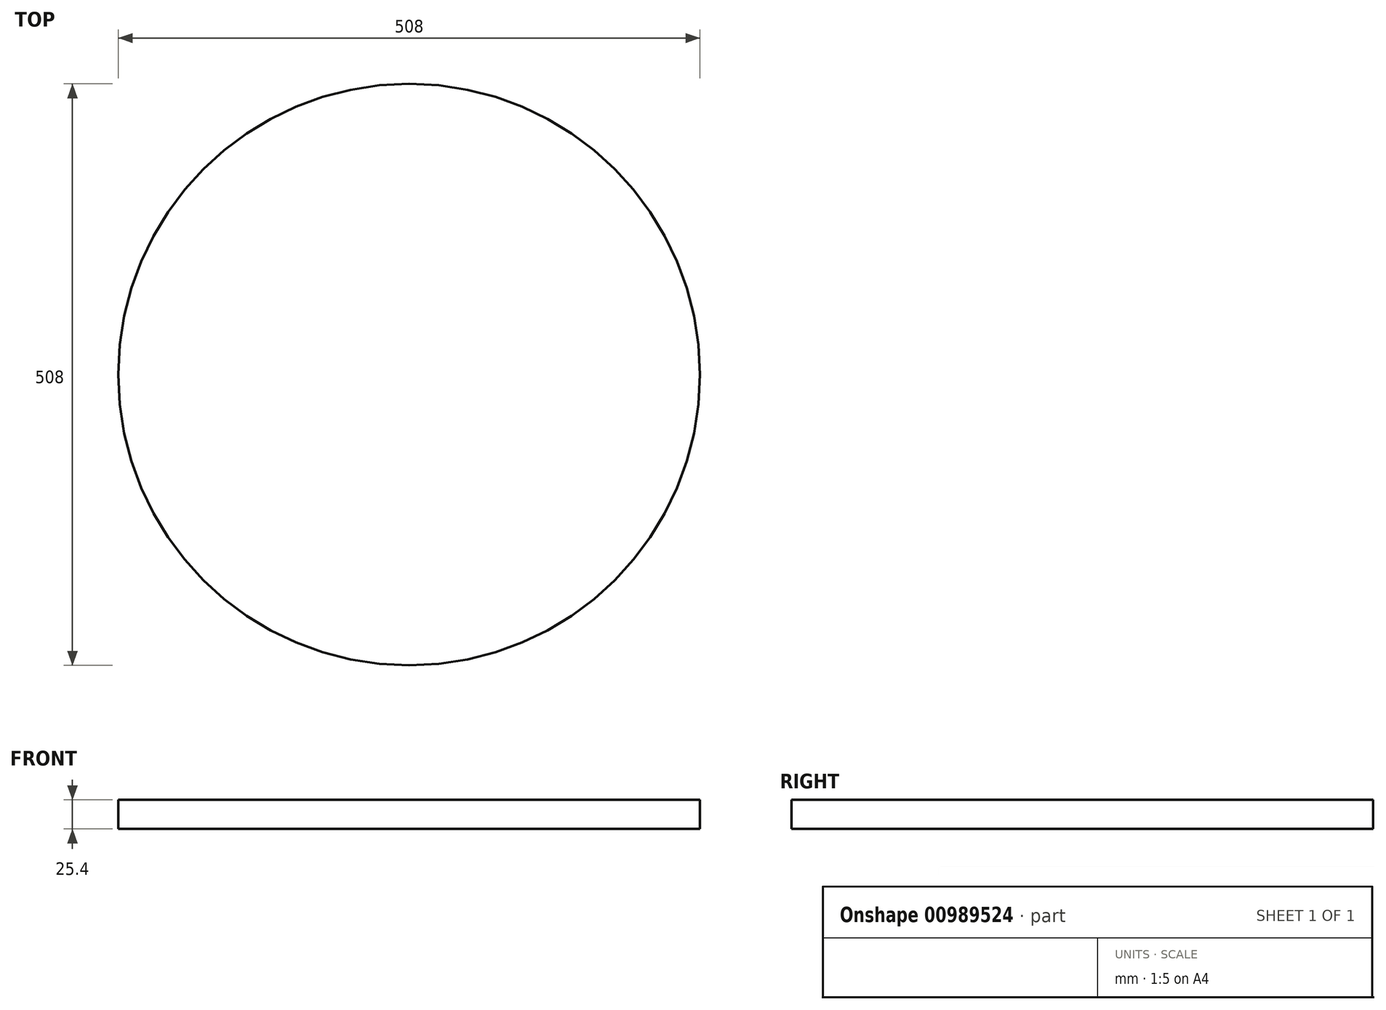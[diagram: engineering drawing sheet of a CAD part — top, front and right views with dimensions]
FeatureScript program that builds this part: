
annotation { "Feature Type Name" : "Feature", "Feature Type Description" : "" }
export const myFeature = defineFeature(function(context is Context, id is Id, definition is map)
    precondition{}
    {
        {
            var Q0;
            Q0=qCreatedBy(makeId("Top.planeOp"),FACE);
            var sketch = newSketch(context, id + "F0", { "sketchPlane" : qUnion([Q0])});
            skCircle(sketch, "E0", {"center": v(0, 0) * mm, "radius": 254 * mm});
            skSolve(sketch);
        }
        {
            var Q0;
            Q0 = qSketchRegion(id + "F0", true);
            extrude(context, id + "F1", {"entities" : qUnion([Q0]), "depth" : 25.4 * mm, "offsetDistance" : 25.4 * mm});
        }
    });
